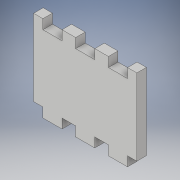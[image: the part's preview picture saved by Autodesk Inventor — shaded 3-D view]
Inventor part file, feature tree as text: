
AUTODESK INVENTOR PART (.ipt)
format: ipt  version: 2018 (Build 220112000, 112)  size: 132,608 bytes
history: native  units: in
note: dims shown in document units (in); Inventor stores cm internally (conversion verified against a paired STEP export)
features: extrude x2, sketch x2
ambient origin geometry x8: Origin, YZ Plane, XZ Plane, XY Plane, X Axis, Y Axis, Z Axis, Center Point
bodies: Solid1 (feature_tree)
feature tree (4):
  extrude  "Extrusion1"  Depth=2.0in
  extrude  "Extrusion2"  Depth=0.25in TaperAngle=0.0deg
  sketch  "Sketch1"  dims[d0=2.7in d1=2.0in]
  sketch  "Sketch2"  dims[d9=0.25in d10=0.0in d12=0.25in d13=0.0in]
